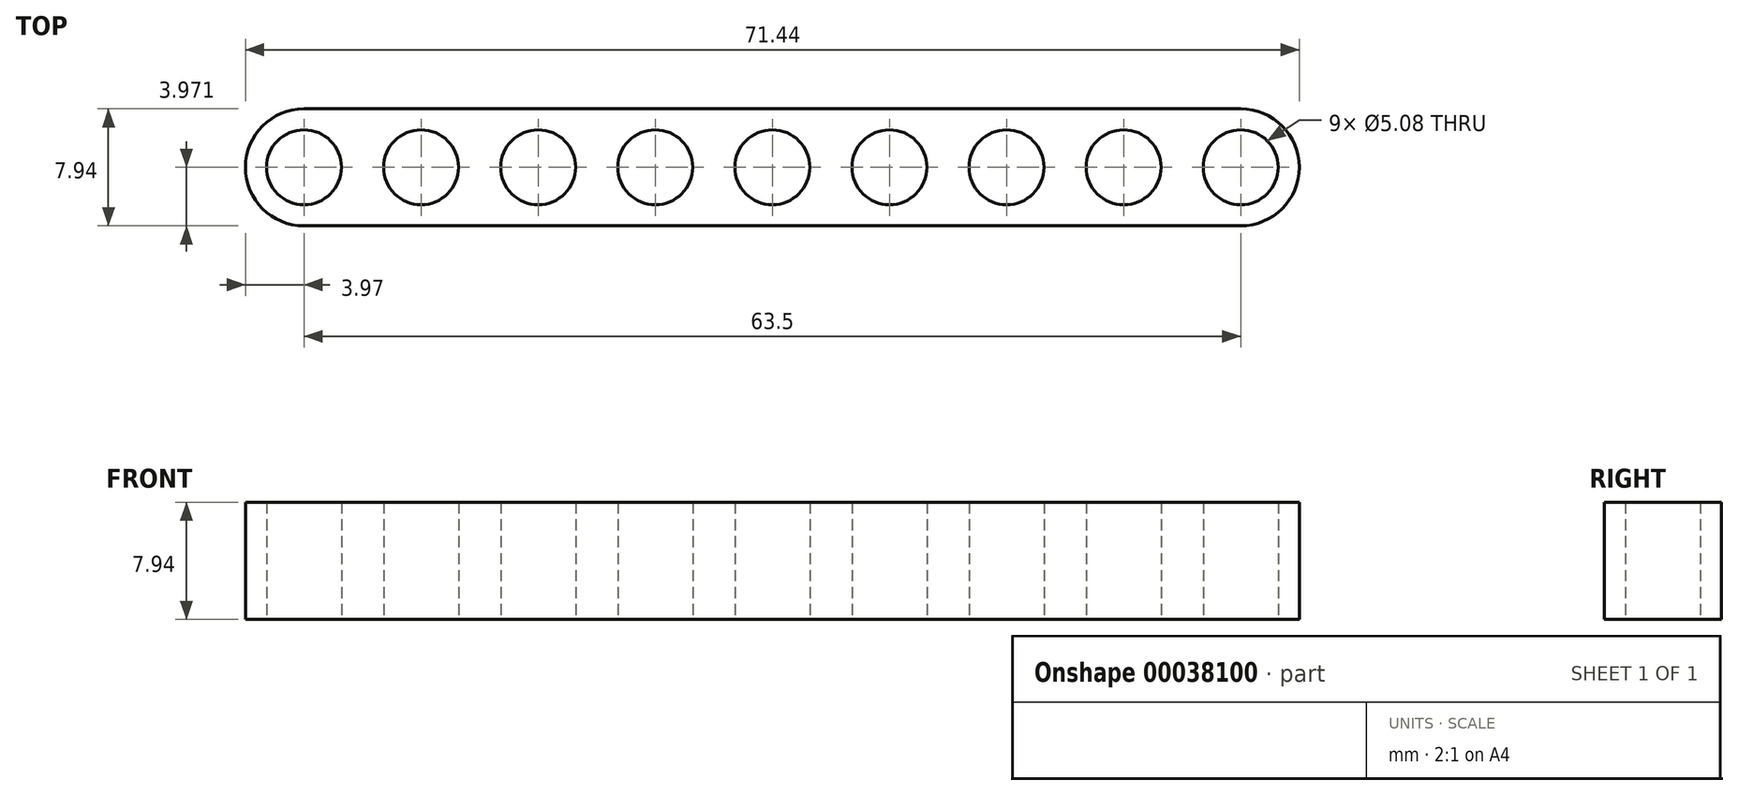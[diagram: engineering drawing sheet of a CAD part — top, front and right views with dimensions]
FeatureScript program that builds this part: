
annotation { "Feature Type Name" : "Feature", "Feature Type Description" : "" }
export const myFeature = defineFeature(function(context is Context, id is Id, definition is map)
    precondition{}
    {
        {
            var Q0;
            Q0=qCreatedBy(makeId("Top.planeOp"),FACE);
            var sketch = newSketch(context, id + "F0", { "sketchPlane" : qUnion([Q0])});
            skLineSegment(sketch, "E0.bottom", {"start": v(0, 0) * mm, "end": v(63.5, 0) * mm});
            skLineSegment(sketch, "E0.top", {"start": v(0, -7.94) * mm, "end": v(63.5, -7.94) * mm});
            skLineSegment(sketch, "E0.left", {"start": v(0, 0) * mm, "end": v(0, -7.94) * mm});
            skLineSegment(sketch, "E1", {"start": v(0, -3.97) * mm, "end": v(7.94, -3.97) * mm, "construction": true});
            skLineSegment(sketch, "E2", {"start": v(7.94, -3.97) * mm, "end": v(15.88, -3.97) * mm, "construction": true});
            skLineSegment(sketch, "E3", {"start": v(15.88, -3.97) * mm, "end": v(23.81, -3.97) * mm, "construction": true});
            skLineSegment(sketch, "E4", {"start": v(23.81, -3.97) * mm, "end": v(31.75, -3.97) * mm, "construction": true});
            skArc(sketch, "E5", {"start": v(0, 0) * mm, "mid": v(-3.97, -3.97) * mm, "end": v(0, -7.94) * mm});
            skCircle(sketch, "E6", {"center": v(0, -3.97) * mm, "radius": 2.54 * mm});
            skCircle(sketch, "E7", {"center": v(7.94, -3.97) * mm, "radius": 2.54 * mm});
            skCircle(sketch, "E8", {"center": v(15.88, -3.97) * mm, "radius": 2.54 * mm});
            skCircle(sketch, "E9", {"center": v(23.81, -3.97) * mm, "radius": 2.54 * mm});
            skCircle(sketch, "E10", {"center": v(31.75, -3.97) * mm, "radius": 2.54 * mm});
            skLineSegment(sketch, "E11", {"start": v(31.75, -3.97) * mm, "end": v(39.69, -3.97) * mm, "construction": true});
            skLineSegment(sketch, "E12", {"start": v(39.69, -3.97) * mm, "end": v(47.63, -3.97) * mm, "construction": true});
            skLineSegment(sketch, "E13", {"start": v(47.63, -3.97) * mm, "end": v(55.56, -3.97) * mm, "construction": true});
            skLineSegment(sketch, "E14", {"start": v(55.56, -3.97) * mm, "end": v(63.5, -3.97) * mm, "construction": true});
            skLineSegment(sketch, "E15", {"start": v(63.5, 0) * mm, "end": v(63.5, -7.94) * mm, "construction": true});
            skArc(sketch, "E16", {"start": v(63.5, -7.94) * mm, "mid": v(67.47, -3.97) * mm, "end": v(63.5, 0) * mm});
            skCircle(sketch, "E17", {"center": v(39.69, -3.97) * mm, "radius": 2.54 * mm});
            skCircle(sketch, "E18", {"center": v(47.63, -3.97) * mm, "radius": 2.54 * mm});
            skCircle(sketch, "E19", {"center": v(55.56, -3.97) * mm, "radius": 2.54 * mm});
            skCircle(sketch, "E20", {"center": v(63.5, -3.97) * mm, "radius": 2.54 * mm});
            skSolve(sketch);
        }
        {
            var Q0;
            Q0=qSketchRegion(id+"F0",true);
            extrude(context, id + "F1", {"entities" : qUnion([Q0]), "depth" : 7.94 * mm});
        }
    });
